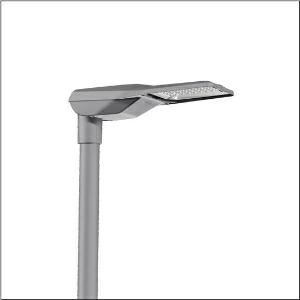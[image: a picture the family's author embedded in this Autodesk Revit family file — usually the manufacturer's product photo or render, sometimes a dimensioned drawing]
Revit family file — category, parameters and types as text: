
# Revit family: streetlight_sl_21_iq_mini___p1_0a_5xe2a41g08gb_a1a0
name_source: partatom
category: Lighting Fixtures
units: mm (PartAtom-declared; Revit-internal decimal feet)

## family parameters
Cut with Voids When Loaded = No
Host = Face
Light Source = No
Part Type = Normal
Room Calculation Point = No
Round Connector Dimension = Use Diameter
Shared = No

## types (1)
- --- (1 x LED, 5920 lm, 37.1 W, 4000K)
    Apparent Load = 37 VA
    CIE Flux Codes = 21 50 90 100 100
    Color Rendering = 70
    Color Temperature = 4000K
    Default Elevation = 1800 mm
    Description = Streetlight SL 21 iQ mini, mast luminaire, primary light control with lens, of PMMA, primary optical cover: cover, of toughened safety glass, transparent, light distribution: P1.0a, light emission: direct distribution, primary light characteristic: asymmetric, installation type: post-top, side-entry, LED, High Power LED, rated luminous flux: 5.920lm, luminous efficacy: 160lm/W, light colour: 740, colour temperature: 4000K, control: Street-Remote, Auto-Match, Temp-Guard, Lumen-Switch, Night-Set, Smart-Wire, Light-Fading, Desk-Remote (wireless, voltage-free reading and setting of iQ features in the workshop via application-optimized NFC function/RFID function), optimised constant luminous flux control (CLO 2.0), pre-setting: linear dimming characteristic, mains connection: 220..240V, AC, 50/60Hz, start of lifetime: 37W, end of service life: 39W, reduction: 18W, luminaire housing, of diecast aluminium, powder-coated, Siteco® metallic grey (DB 702S), corrosivity category C5 mid according to DIN EN ISO 12944, please order mast flange separately, inclination adjustable: 0°, 5°, 10°, 15°, sealing non-destructively replaceable, multi-level sealing system, length: 628mm, width: 235mm, height: 110mm, mast flange for spigot size: 42mm (side-entry): 5XC10008XM4, 60/48mm (side-entry/post-top): 5XC10108XM2, 76/60mm (side-entry/post-top): 5XC10108XM1, protection rating (complete): IP66, insulation class (complete): insulation class II (safety insulation), certification: CE, ENEC, ENEC+, VDE, impact resistance: IK09, permissible operating ambient temperature for outdoor applications: -40..+50°C, standard-compliant lighting for roads and squares, packaging unit: 1 piece

Light Distribution: P1.0a
    Height = 110 mm
    Lamp = 1 x LED
    Lamp Light Flux = 5920 lm
    Lamp Power = 37.1 W
    Lamp count = 1
    Length = 625 mm
    Luminous efficacy = 160 lm/W
    Manufacturer = Siteco
    ModVariant = No
    Model = 5XE2A41G08GB
    Number of Poles = 1
    OnlyDefault = Yes
    Power Factor = 1
    Product Name = Streetlight SL 21 iQ mini | P1.0a
    Product group = mast luminaire | pylon top
    ProductGroupID = 6100
    Protection Class = Protection class II
    Protection Degree = IP 66
    RLX_Detail_Level = 1
    RLX_Emergency_Light_Flux = 0 lm
    RLX_Emergency_Type = 0
    RLX_Emergency_Type_DB = No
    RlxData = <blob elided: 103689 chars, md5=54345c17>
    Socket = socket
    Standby Power = 0 W
    System Light Flux = 5920 lm
    System Power = 37 W
    Type Comments = factory setting: luminous flux: 100 % | dim-lin: 254 | 385 mA
    Type Image = l_1003519.jpg
    URL = http://relux.com
    VarID = @adj_158625
    Voltage = 0 V
    Weight = 0.00 kg
    Width = 234 mm

## geometry (parser evidence)
native form markers: Blend x4, Sweep x10
no freeform markers — native parametric forms only
